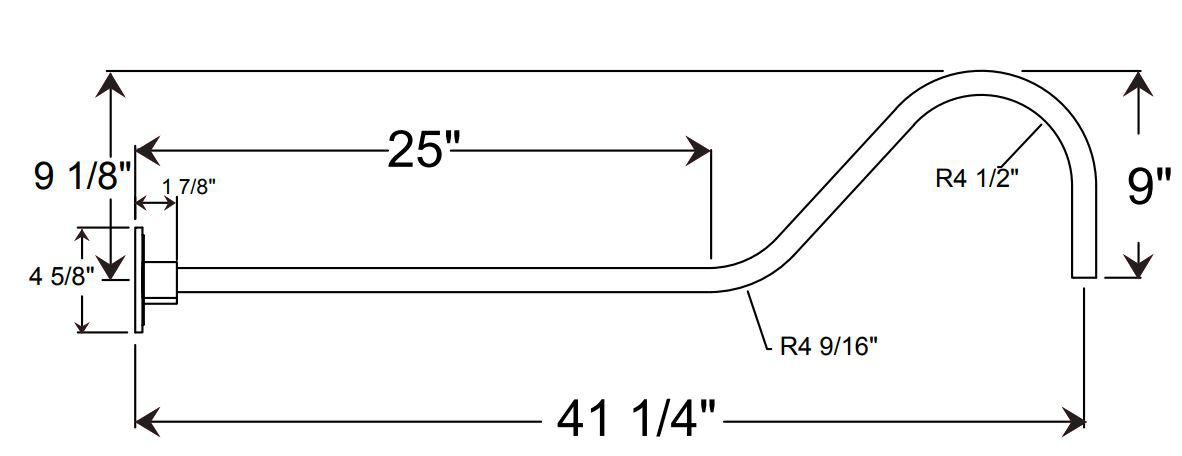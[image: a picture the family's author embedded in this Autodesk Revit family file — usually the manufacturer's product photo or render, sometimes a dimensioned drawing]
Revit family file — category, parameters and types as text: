
# Revit family: MILKCAN(8,10,12,18) LED
name_source: partatom
category: Lighting Fixtures
units: mm (PartAtom-declared; Revit-internal decimal feet)

## family parameters
Always vertical = Yes
Cut with Voids When Loaded = No
Light Source = Yes
OmniClass Number = 23.80.70.00
OmniClass Title = Lighting
Part Type = Normal
Room Calculation Point = No
Round Connector Dimension = Use Diameter
Shared = No
Work Plane-Based = No

## types (4) — shared parameters
Body Colour = Spun aluminium
Body Material = body
CRI = >90
Color Filter = 16777215
Construction Material = Heavy Duty spun aluminum.
Default Elevation = 0' - 0"
Description = 120-277 Voltage
Dimming = 1%
Dimming Lamp Color Temperature Shift = <None>
Efficiency = 65-125 lumens per watt
Lamp = LED
Life = L70 50,000 hours
Load Classification = Lighting
Manufacturer = ANP Lighting
Photometric Web File = MC18M024LDN40K.ies
Power Factor = 1
Tilt Angle = 90.00°
URL = https://www.anplighting.com
Voltage = 277 V
Warranty = 5 year limited warranty

## per-type parameters (varying)
| type | Apparent Load | Fixture Diameter | Fixture Height | MC10 | MC12 | MC18 | MC8 | Wattage Comments | Weight |
| MC08 | 9 VA | 0' - 8" | 0' - 4" | No | No | No | Yes | 9W | 1 lbs |
| MC10 | 10 VA | 0' - 10" | 0' - 4" | Yes | No | No | No | 10W | 1 lbs |
| MC12 | 16 VA | 1' - 0" | 0' - 5" | No | Yes | No | No | 16W | 1.5 lbs |
| MC18 | 24 VA | 1' - 6" | 0' - 6" | No | No | Yes | No | 24W | 2 lbs |

note: column(s) folded — value = type name in every type: Model

## geometry (parser evidence)
native form markers: Sweep x29
no freeform markers — native parametric forms only
